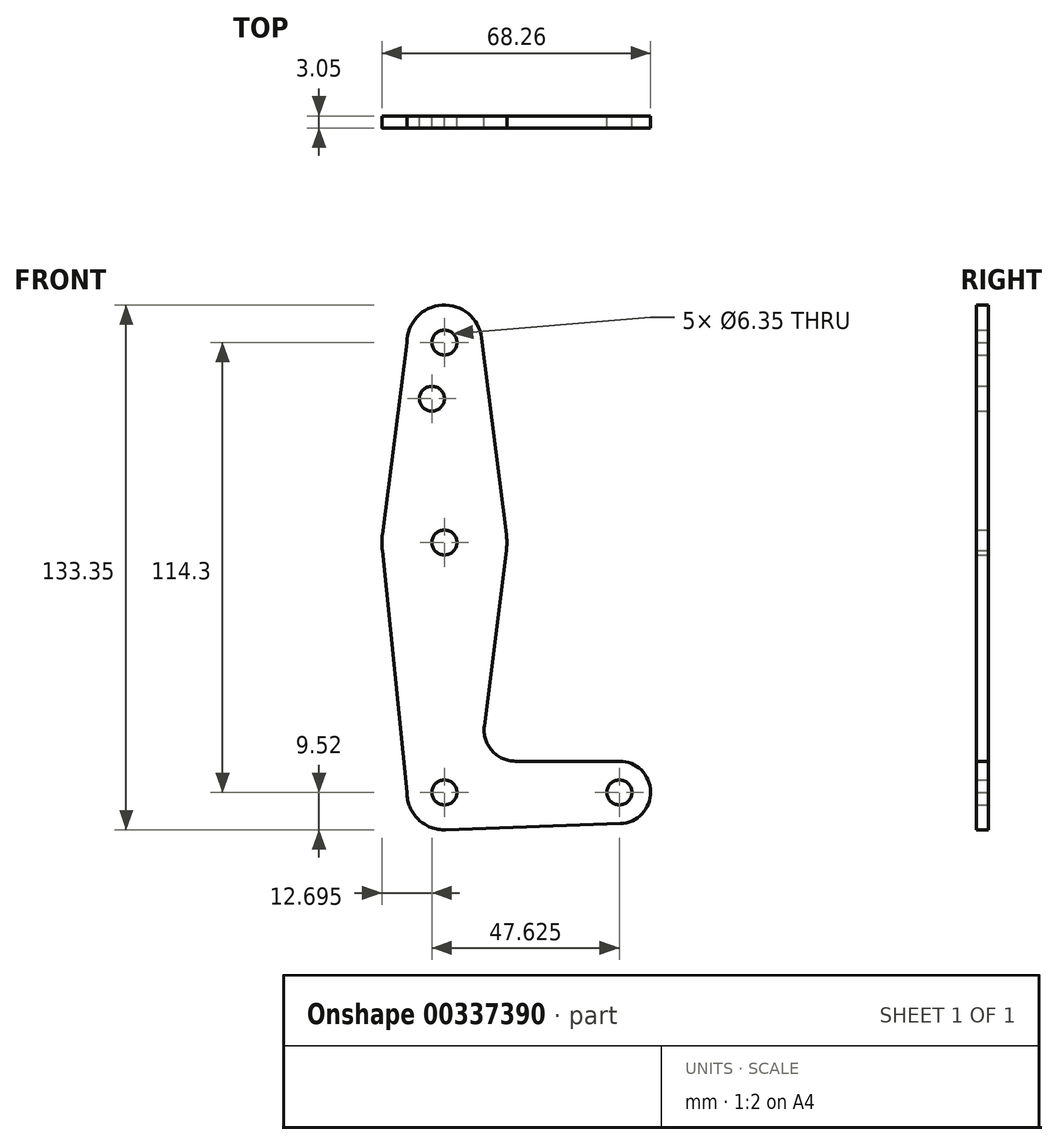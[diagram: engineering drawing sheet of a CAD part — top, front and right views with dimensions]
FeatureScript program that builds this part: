
annotation { "Feature Type Name" : "Feature", "Feature Type Description" : "" }
export const myFeature = defineFeature(function(context is Context, id is Id, definition is map)
    precondition{}
    {
        {
            var Q0;
            Q0=qCreatedBy(makeId("Front.planeOp"),FACE);
            var sketch = newSketch(context, id + "F0", { "sketchPlane" : qUnion([Q0])});
            skLineSegment(sketch, "E0", {"start": v(44.45, 0) * mm, "end": v(0, 0) * mm, "construction": true});
            skLineSegment(sketch, "E1", {"start": v(0, 0) * mm, "end": v(0, 114.3) * mm, "construction": true});
            skCircle(sketch, "E2", {"center": v(0, 114.3) * mm, "radius": 9.53 * mm});
            skCircle(sketch, "E3", {"center": v(0, 0) * mm, "radius": 9.53 * mm});
            skCircle(sketch, "E4", {"center": v(44.45, 0) * mm, "radius": 7.94 * mm});
            skCircle(sketch, "E5", {"center": v(0, 63.5) * mm, "radius": 15.88 * mm});
            skLineSegment(sketch, "E6", {"start": v(-9.53, 114.3) * mm, "end": v(-15.75, 65.5) * mm});
            skLineSegment(sketch, "E7", {"start": v(-9.53, 0) * mm, "end": v(-15.75, 61.5) * mm});
            skLineSegment(sketch, "E8", {"start": v(9.45, 115.5) * mm, "end": v(15.75, 65.48) * mm});
            skLineSegment(sketch, "E9", {"start": v(10.13, 16.88) * mm, "end": v(15.75, 61.52) * mm});
            skLineSegment(sketch, "E10", {"start": v(18.01, 7.94) * mm, "end": v(44.45, 7.94) * mm});
            skLineSegment(sketch, "E11", {"start": v(0.34, -9.52) * mm, "end": v(44.73, -7.93) * mm});
            skCircle(sketch, "E12", {"center": v(0, 114.3) * mm, "radius": 3.18 * mm});
            skCircle(sketch, "E13", {"center": v(-3.18, 100.03) * mm, "radius": 3.18 * mm});
            skCircle(sketch, "E14", {"center": v(0, 63.5) * mm, "radius": 3.18 * mm});
            skCircle(sketch, "E15", {"center": v(0, 0) * mm, "radius": 3.18 * mm});
            skCircle(sketch, "E16", {"center": v(44.45, 0) * mm, "radius": 3.18 * mm});
            skArc(sketch, "E17.filletArc", {"start": v(10.13, 16.88) * mm, "mid": v(12.05, 10.63) * mm, "end": v(18.01, 7.94) * mm});
            skSolve(sketch);
        }
        {
            var Q0;
            Q0 = qSketchRegion(id + "F0", true);
            extrude(context, id + "F1", {"entities" : qUnion([Q0]), "depth" : 3.05 * mm});
        }
    });
